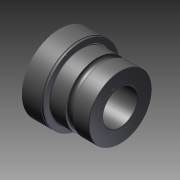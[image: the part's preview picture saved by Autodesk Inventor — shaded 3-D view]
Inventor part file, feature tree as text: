
AUTODESK INVENTOR PART (.ipt)
format: ipt  version: 2011 SP1 (Build 150282100, 282)  size: 225,280 bytes
history: native  units: mm
features: other x7, revolve x1, sketch x1
ambient origin geometry x8: Origin, YZ Plane, XZ Plane, XY Plane, X Axis, Y Axis, Z Axis, Center Point
bodies: Solid1 (feature_tree)
feature tree (9):
  revolve  "Revolution1"  [1 undecoded]
  other  "to_housing_XY"
  other  "to_housing_YZ"
  other  "to_housing_ZX"
  other  "to_housing_X"
  other  "to_housing_Y"
  other  "to_housing_Z"
  other  "to_housing_Center"
  sketch  "Sketch_1"  dims[d0=360.0deg d1=0.0mm]
note: 1 required parameter value undecoded (feature->parameter linkage not recoverable at this tier; creation-order binding heuristic only, values carry confidence <= 0.55)
